# Revit family: Reece_Toilet_Roca_Inspira_Pan Back to Wall_In Wash_Rimless_Heated Seat
name_source: partatom
category: Plumbing Fixtures
revit_build: Autodesk Revit 2018 (Build: 20190510_1515(x64)
units: mm (PartAtom-declared; Revit-internal decimal feet)

## family parameters
Always vertical = Yes
Cut with Voids When Loaded = No
Part Type = Normal
Room Calculation Point = No
Round Connector Dimension = Use Diameter
Shared = No
Work Plane-Based = No

## types (1)
- Bottom Inlet_Vitreous China_White
    Description = Roca In-Wash Inspira Rimless Back To Wall Pan with Heated Seat (4 Star)
    Disclaimer = THIS FILE IS THE PROPERTY OF THE REECE GROUP. IT MAY NOT BE REPRODUCED, REVERSE-ENGINEERED OR MODIFIED. ANY REPUBLICATION, TRANSMISSION OR DISTRIBUTION FOR THE PURPOSE OF COMMERCIALLY EXPLOITING THE FILES IS PROHIBITED.
    Keynote = Product #9510069, Reece_Toilet_Roca_Inspira_Pan Back to Wall_In Wash_Rimless_Heated Seat - Bottom Inlet_Vitreous China_White
    Manufacturer = Roca
    Model = Inspira
    Reece_Back_Outlet_Offset = 180 mm  [stored 0.590551 ft]
    Reece_Bottom_Inlet = 12 mm  [stored 0.0393701 ft]
    Reece_Bottom_Outlet_Offset = 150 mm
    Reece_Detail_Additional = In-Wash, Heated Seat
    Reece_Detail_Disclaimer = THIS FILE IS THE PROPERTY OF THE REECE GROUP. IT MAY NOT BE REPRODUCED, REVERSE-ENGINEERED OR MODIFIED. ANY REPUBLICATION, TRANSMISSION OR DISTRIBUTION FOR THE PURPOSE OF COMMERCIALLY EXPLOITING THE FILES IS PROHIBITED.
    Reece_Detail_Installation = Pan Back to Wall
    Reece_Detail_Shape = Rimless
    Reece_Detail_Type = Toilet
    Reece_Material_Colour = Reece_Light_LED_White
    Reece_Material_Main = Reece_Brass_Chrome
    Reece_Material_Pan = Reece_Vitreous China_White
    Reece_Material_Seat = Reece_Vitreous China_White
    Reece_Material_Secondary = Reece_Plastic_White
    Reece_Overall_Height = 485 mm  [stored 1.59121 ft]
    Reece_Overall_Projection = 585 mm  [stored 1.91929 ft]
    Reece_Overall_Width = 380 mm  [stored 1.24672 ft]
    Reece_P_Trap = 102 mm  [stored 0.334646 ft]
    Reece_Pan_Height = 405 mm  [stored 1.32874 ft]
    Reece_Product_Brand = Roca
    Reece_Product_Description = Roca In-Wash Inspira Rimless Back To Wall Pan with Heated Seat (4 Star)
    Reece_Product_Mount = Floor Mounted
    Reece_Product_Number = 9510069
    Reece_Product_Sub Brand = Inspira
    Reece_Product_Web Page = https://www.reece.com.au
    Reece_S_Trap = 102 mm  [stored 0.334646 ft]
    URL = https://www.reece.com.au

note: [stored X ft] marks values corroborated as IEEE doubles in the binary element streams (Revit-internal decimal feet)

## geometry (parser evidence)
native form markers: Sweep x8
no freeform markers — native parametric forms only
